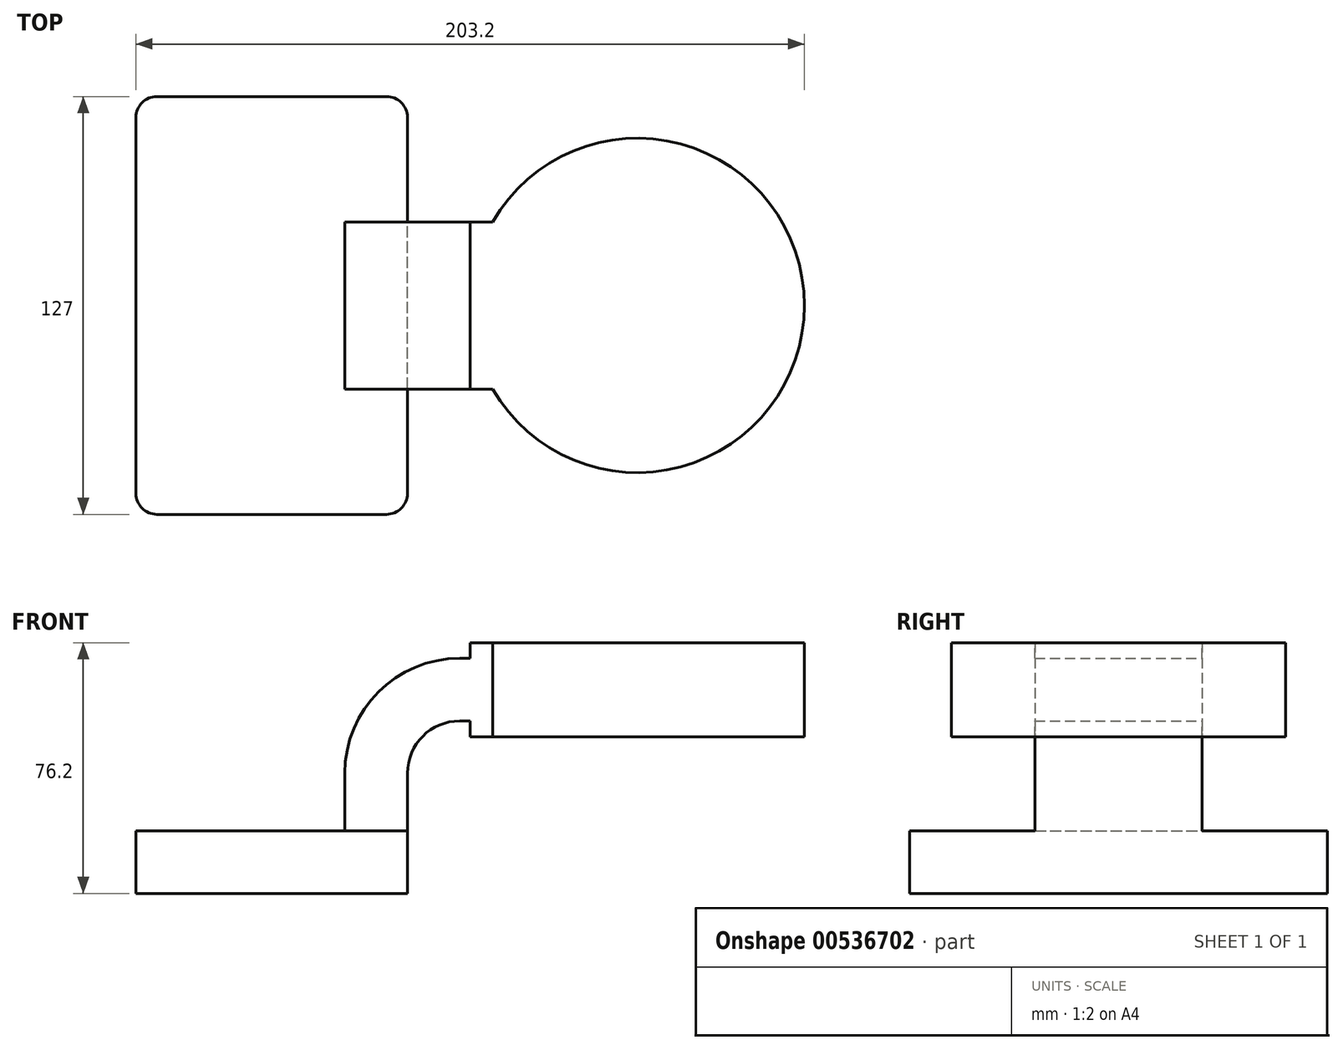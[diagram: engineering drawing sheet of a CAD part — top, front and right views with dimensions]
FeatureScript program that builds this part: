
annotation { "Feature Type Name" : "Feature", "Feature Type Description" : "" }
export const myFeature = defineFeature(function(context is Context, id is Id, definition is map)
    precondition{}
    {
        {
            var Q0;
            Q0=qCreatedBy(makeId("Front.planeOp"),FACE);
            var sketch = newSketch(context, id + "F0", { "sketchPlane" : qUnion([Q0])});
            skLineSegment(sketch, "E0.bottom", {"start": v(-41.28, 9.52) * mm, "end": v(41.28, 9.53) * mm});
            skLineSegment(sketch, "E0.top", {"start": v(-41.28, -9.53) * mm, "end": v(41.28, -9.53) * mm});
            skLineSegment(sketch, "E0.left", {"start": v(-41.28, 9.52) * mm, "end": v(-41.28, -9.53) * mm});
            skLineSegment(sketch, "E0.right", {"start": v(41.28, 9.53) * mm, "end": v(41.28, -9.52) * mm});
            skPoint(sketch, "E0.middle", {"position": v(0, 0) * mm});
            skLineSegment(sketch, "E1.bottom", {"start": v(60.33, 38.1) * mm, "end": v(111.12, 38.1) * mm});
            skLineSegment(sketch, "E1.top", {"start": v(60.32, 66.68) * mm, "end": v(111.12, 66.68) * mm});
            skLineSegment(sketch, "E1.left", {"start": v(60.33, 38.1) * mm, "end": v(60.32, 66.68) * mm});
            skLineSegment(sketch, "E1.right", {"start": v(111.12, 38.1) * mm, "end": v(111.12, 66.68) * mm});
            skPoint(sketch, "E1.middle", {"position": v(85.72, 52.39) * mm});
            skLineSegment(sketch, "E2", {"start": v(41.27, 9.53) * mm, "end": v(41.27, 27) * mm});
            skArc(sketch, "E3", {"start": v(41.27, 27) * mm, "mid": v(45.92, 38.23) * mm, "end": v(57.15, 42.88) * mm});
            skLineSegment(sketch, "E4", {"start": v(57.15, 42.88) * mm, "end": v(86.22, 42.88) * mm});
            skLineSegment(sketch, "E5.0", {"start": v(57.15, 61.93) * mm, "end": v(86.22, 61.93) * mm});
            skArc(sketch, "E5.1", {"start": v(22.22, 27) * mm, "mid": v(32.45, 51.7) * mm, "end": v(57.15, 61.93) * mm});
            skLineSegment(sketch, "E5.2", {"start": v(22.22, 9.53) * mm, "end": v(22.22, 27) * mm});
            skFitSpline(sketch, "E6", {"points": [v(-41.28, 9.52) * mm, v(57.15, 61.93) * mm], "startDerivative": vector(4.5, 134.67) * mm, "endDerivative": vector(73.56, -18.2) * mm});
            skSolve(sketch);
        }
        {
            var Q0;
            Q0=makeQuery(id+"F0.imprint","IMPRINT",FACE,{"disambiguationData":[TD([[makeQuery(id+"F0.imprint","IMPRINT",EDGE,{"derivedFrom":sQuery(id+"F0.wireOp",EDGE,"E0.top")}),1.0]])]});
            extrude(context, id + "F1", {"entities" : qUnion([Q0]), "endBound" : BoundingType.SYMMETRIC, "depth" : 127 * mm, "offsetDistance" : 25.4 * mm});
        }
        {
            var Q0;
            {var subQ1=sQuery(id+"F0.wireOp",EDGE,"E2");Q0=makeQuery(id+"F0.imprint","IMPRINT",FACE,{"disambiguationData":[TD([[makeQuery(id+"F0.imprint","IMPRINT",EDGE,{"derivedFrom":subQ1}),1.0]])]});}
            var Q1;
            {var subQ3=sQuery(id+"F0.wireOp",EDGE,"E1.bottom");Q1=makeQuery(id+"F0.imprint","IMPRINT",FACE,{"disambiguationData":[TD([[makeQuery(id+"F0.imprint","IMPRINT",EDGE,{"derivedFrom":subQ3}),1.0]])]});}
            extrude(context, id + "F2", {"entities" : qUnion([Q0, Q1]), "operationType" : NewBodyOperationType.ADD, "endBound" : BoundingType.SYMMETRIC, "depth" : 50.8 * mm, "offsetDistance" : 25.4 * mm});
        }
        {
            var Q0;
            Q0=makeQuery(id+"F0.imprint","IMPRINT",FACE,{"disambiguationData":[TD([[makeQuery(id+"F0.imprint","IMPRINT",EDGE,{"derivedFrom":sQuery(id+"F0.wireOp",EDGE,"E5.1")}),1.0]])]});
            extrude(context, id + "F3", {"entities" : qUnion([Q0]), "operationType" : NewBodyOperationType.ADD, "endBound" : BoundingType.SYMMETRIC, "depth" : 15.88 * mm, "offsetDistance" : 25.4 * mm});
        }
        {
            var Q0;
            {var subQ3=sQuery(id+"F0.wireOp",EDGE,"E1.bottom");Q0=makeQuery(id+"F0.imprint","IMPRINT",FACE,{"disambiguationData":[TD([[makeQuery(id+"F0.imprint","IMPRINT",EDGE,{"derivedFrom":subQ3}),1.0]])]});}
            var Q1;
            Q1=sQuery(id+"F0.wireOp",EDGE,"E1.right");
            revolve(context, id + "F4", {"operationType" : NewBodyOperationType.ADD, "entities" : qUnion([Q0]), "axis" : qUnion([Q1]), "revolveType" : RevolveType.FULL});
        }
        {
            var Q0;
            Q0=makeQuery(id+"F1.opExtrude","CAP_EDGE",EDGE,{"disambiguationData":[OSD([sQuery(id+"F0.wireOp",EDGE,"E0.left")])],"isStart":false});
            var Q1;
            Q1=makeQuery(id+"F1.opExtrude","CAP_EDGE",EDGE,{"disambiguationData":[OSD([sQuery(id+"F0.wireOp",EDGE,"E0.right")])],"isStart":false});
            var Q2;
            Q2=makeQuery(id+"F1.opExtrude","CAP_EDGE",EDGE,{"disambiguationData":[OSD([sQuery(id+"F0.wireOp",EDGE,"E0.right")])],"isStart":true});
            var Q3;
            Q3=makeQuery(id+"F1.opExtrude","CAP_EDGE",EDGE,{"disambiguationData":[OSD([sQuery(id+"F0.wireOp",EDGE,"E0.left")])],"isStart":true});
            fillet(context, id + "F5", {"entities" : qUnion([Q0, Q1, Q2, Q3]), "radius" : 6.35 * mm, "tangentPropagation" : true, "allowEdgeOverflow" : false});
        }
    });
